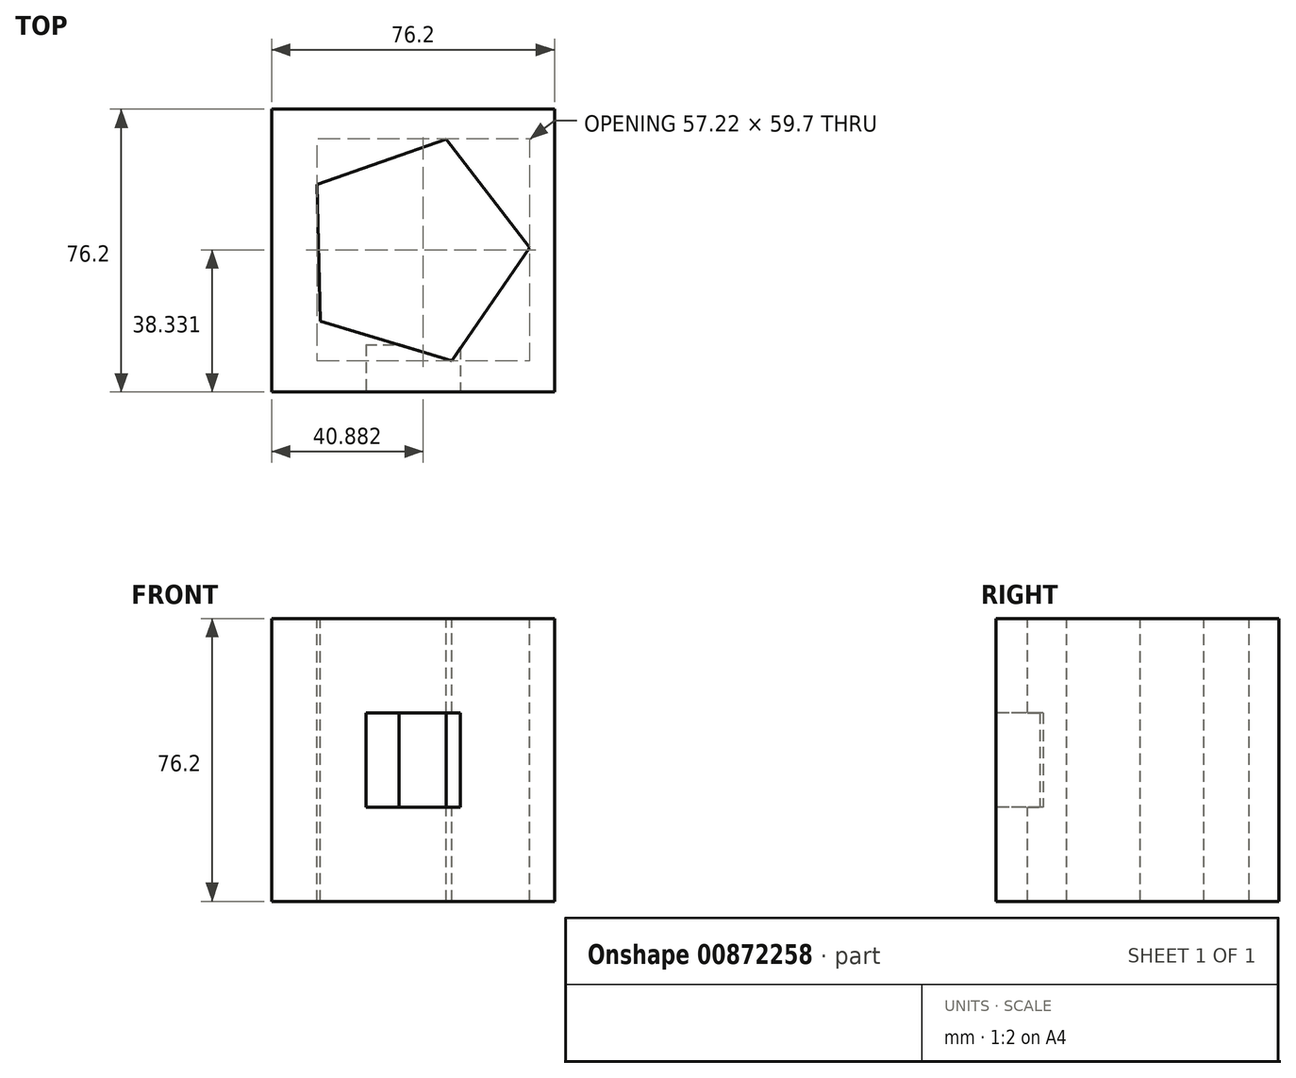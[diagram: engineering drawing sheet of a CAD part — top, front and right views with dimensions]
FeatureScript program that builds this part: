
annotation { "Feature Type Name" : "Feature", "Feature Type Description" : "" }
export const myFeature = defineFeature(function(context is Context, id is Id, definition is map)
    precondition{}
    {
        {
            var Q0;
            Q0=qCreatedBy(makeId("Top.planeOp"),FACE);
            var sketch = newSketch(context, id + "F0", { "sketchPlane" : qUnion([Q0])});
            skLineSegment(sketch, "E0.bottom", {"start": v(-71.4, 67.72) * mm, "end": v(4.8, 67.72) * mm});
            skLineSegment(sketch, "E0.top", {"start": v(-71.4, -8.48) * mm, "end": v(4.8, -8.48) * mm});
            skLineSegment(sketch, "E0.left", {"start": v(-71.4, 67.72) * mm, "end": v(-71.4, -8.48) * mm});
            skLineSegment(sketch, "E0.right", {"start": v(4.8, 67.72) * mm, "end": v(4.8, -8.48) * mm});
            skSolve(sketch);
        }
        {
            var Q0;
            Q0=makeQuery(id+"F0.imprint","IMPRINT",FACE,{"disambiguationData":[TD([[makeQuery(id+"F0.imprint","IMPRINT",EDGE,{"derivedFrom":sQuery(id+"F0.wireOp",EDGE,"E0.bottom")}),-1.0]])]});
            extrude(context, id + "F1", {"entities" : qUnion([Q0]), "depth" : 76.2 * mm, "offsetDistance" : 25.4 * mm});
        }
        {
            var Q0;
            Q0=makeQuery(id+"F1.opExtrude","CAP_FACE",FACE,{"disambiguationData":[OSD([sQuery(id+"F0.wireOp",EDGE,"E0.bottom"),sQuery(id+"F0.wireOp",EDGE,"E0.top"),sQuery(id+"F0.wireOp",EDGE,"E0.left"),sQuery(id+"F0.wireOp",EDGE,"E0.right")])],"isStart":false});
            var sketch = newSketch(context, id + "F2", { "sketchPlane" : qUnion([Q0])});
            skCircle(sketch, "E1.cCircle", {"center": v(-33.3, 29.62) * mm, "radius": 25.4 * mm, "construction": true});
            skLineSegment(sketch, "E1.0", {"start": v(-1.9, 30.37) * mm, "end": v(-22.89, 0) * mm});
            skLineSegment(sketch, "E1.1", {"start": v(-22.89, 0) * mm, "end": v(-58.25, 10.57) * mm});
            skLineSegment(sketch, "E1.2", {"start": v(-58.25, 10.57) * mm, "end": v(-59.13, 47.47) * mm});
            skLineSegment(sketch, "E1.3", {"start": v(-59.13, 47.47) * mm, "end": v(-24.3, 59.7) * mm});
            skLineSegment(sketch, "E1.4", {"start": v(-24.3, 59.7) * mm, "end": v(-1.9, 30.37) * mm});
            skPoint(sketch, "E1.0.midPoint", {"position": v(-12.4, 15.18) * mm});
            skSolve(sketch);
        }
        {
            var Q0;
            Q0 = qSketchRegion(id + "F2", true);
            extrude(context, id + "F3", {"entities" : qUnion([Q0]), "operationType" : NewBodyOperationType.REMOVE, "endBound" : BoundingType.THROUGH_ALL, "oppositeDirection" : true, "depth" : 25.4 * mm, "offsetDistance" : 25.4 * mm});
        }
        {
            var Q0;
            Q0=makeQuery(id+"F1.opExtrude","SWEPT_FACE",FACE,{"disambiguationData":[OSD([sQuery(id+"F0.wireOp",EDGE,"E0.top")])]});
            var sketch = newSketch(context, id + "F4", { "sketchPlane" : qUnion([Q0])});
            skLineSegment(sketch, "E2.0", {"start": v(-46, 25.4) * mm, "end": v(-20.6, 25.4) * mm});
            skLineSegment(sketch, "E2.1", {"start": v(-46, 50.8) * mm, "end": v(-46, 25.4) * mm});
            skLineSegment(sketch, "E2.2", {"start": v(-20.6, 50.8) * mm, "end": v(-46, 50.8) * mm});
            skLineSegment(sketch, "E2.3", {"start": v(-20.6, 25.4) * mm, "end": v(-20.6, 50.8) * mm});
            skSolve(sketch);
        }
        {
            var Q0;
            Q0=makeQuery(id+"F4.imprint","IMPRINT",FACE,{"disambiguationData":[TD([[makeQuery(id+"F4.imprint","IMPRINT",EDGE,{"derivedFrom":sQuery(id+"F4.wireOp",EDGE,"E2.0")}),1.0]])]});
            extrude(context, id + "F5", {"entities" : qUnion([Q0]), "operationType" : NewBodyOperationType.REMOVE, "oppositeDirection" : true, "depth" : 12.7 * mm, "offsetDistance" : 25.4 * mm});
        }
    });
